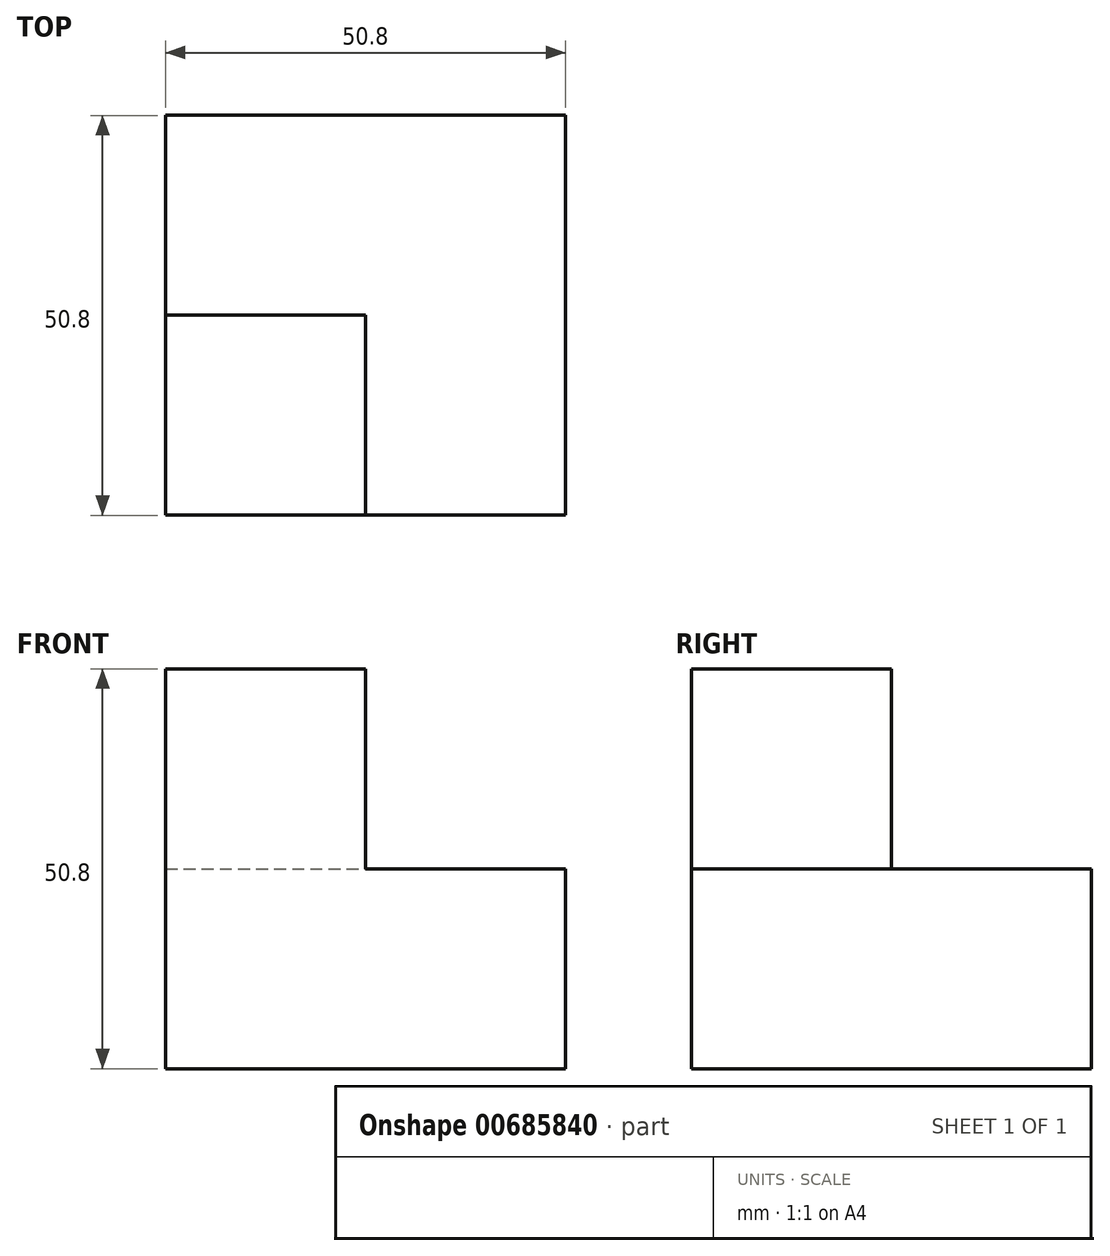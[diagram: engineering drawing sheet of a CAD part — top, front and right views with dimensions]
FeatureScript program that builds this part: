
annotation { "Feature Type Name" : "Feature", "Feature Type Description" : "" }
export const myFeature = defineFeature(function(context is Context, id is Id, definition is map)
    precondition{}
    {
        {
            var Q0;
            Q0=qCreatedBy(makeId("Top.planeOp"),FACE);
            var sketch = newSketch(context, id + "F0", { "sketchPlane" : qUnion([Q0])});
            skLineSegment(sketch, "E0.bottom", {"start": v(-26.73, 25.56) * mm, "end": v(24.07, 25.56) * mm});
            skLineSegment(sketch, "E0.top", {"start": v(-26.73, -25.24) * mm, "end": v(24.07, -25.24) * mm});
            skLineSegment(sketch, "E0.left", {"start": v(-26.73, 25.56) * mm, "end": v(-26.73, -25.24) * mm});
            skLineSegment(sketch, "E0.right", {"start": v(24.07, 25.56) * mm, "end": v(24.07, -25.24) * mm});
            skSolve(sketch);
        }
        {
            var Q0;
            Q0 = qSketchRegion(id + "F0", true);
            extrude(context, id + "F1", {"entities" : qUnion([Q0]), "depth" : 25.4 * mm, "offsetDistance" : 25.4 * mm});
        }
        {
            var Q0;
            Q0=makeQuery(id+"F1.opExtrude","CAP_FACE",FACE,{"disambiguationData":[OSD([sQuery(id+"F0.wireOp",EDGE,"E0.bottom"),sQuery(id+"F0.wireOp",EDGE,"E0.top"),sQuery(id+"F0.wireOp",EDGE,"E0.left"),sQuery(id+"F0.wireOp",EDGE,"E0.right")])],"isStart":false});
            var sketch = newSketch(context, id + "F2", { "sketchPlane" : qUnion([Q0])});
            skLineSegment(sketch, "E1.bottom", {"start": v(-26.73, -25.24) * mm, "end": v(-1.33, -25.24) * mm});
            skLineSegment(sketch, "E1.top", {"start": v(-26.73, 0.16) * mm, "end": v(-1.33, 0.16) * mm});
            skLineSegment(sketch, "E1.left", {"start": v(-26.73, -25.24) * mm, "end": v(-26.73, 0.16) * mm});
            skLineSegment(sketch, "E1.right", {"start": v(-1.33, -25.24) * mm, "end": v(-1.33, 0.16) * mm});
            skSolve(sketch);
        }
        {
            var Q0;
            Q0=makeQuery(id+"F2.imprint","IMPRINT",FACE,{"disambiguationData":[TD([[makeQuery(id+"F2.imprint","IMPRINT",EDGE,{"derivedFrom":sQuery(id+"F2.wireOp",EDGE,"E1.bottom")}),1.0]])]});
            var sketch = newSketch(context, id + "F3", { "sketchPlane" : qUnion([Q0])});
            skSolve(sketch);
        }
        {
            var Q0;
            Q0 = qSketchRegion(id + "F3", true);
            var Q1;
            Q1=makeQuery(id+"F2.imprint","IMPRINT",FACE,{"disambiguationData":[TD([[makeQuery(id+"F2.imprint","IMPRINT",EDGE,{"derivedFrom":sQuery(id+"F2.wireOp",EDGE,"E1.bottom")}),1.0]])]});
            extrude(context, id + "F4", {"entities" : qUnion([Q0, Q1]), "operationType" : NewBodyOperationType.ADD, "depth" : 25.4 * mm, "offsetDistance" : 25.4 * mm});
        }
    });
